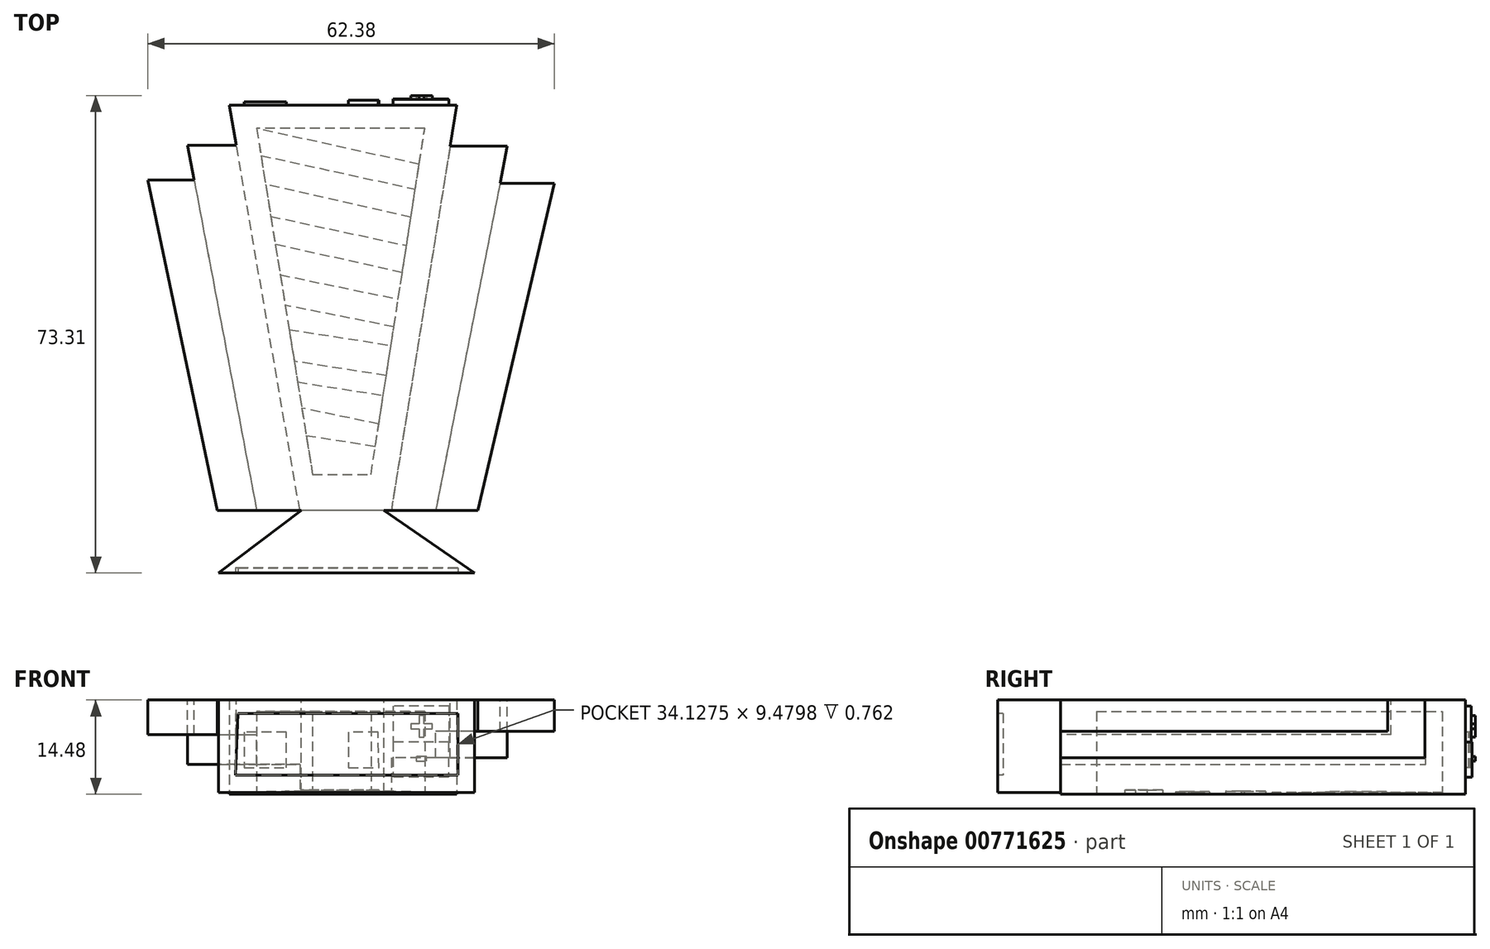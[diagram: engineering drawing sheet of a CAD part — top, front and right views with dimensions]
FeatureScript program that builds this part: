
annotation { "Feature Type Name" : "Feature", "Feature Type Description" : "" }
export const myFeature = defineFeature(function(context is Context, id is Id, definition is map)
    precondition{}
    {
        {
            var Q0;
            Q0=qCreatedBy(makeId("Top.planeOp"),FACE);
            var sketch = newSketch(context, id + "F0", { "sketchPlane" : qUnion([Q0])});
            skLineSegment(sketch, "E0", {"start": v(-16.97, 22.28) * mm, "end": v(17.92, 22.28) * mm});
            skLineSegment(sketch, "E1", {"start": v(17.92, 22.28) * mm, "end": v(7.87, -39.91) * mm});
            skLineSegment(sketch, "E2", {"start": v(7.87, -39.91) * mm, "end": v(-6.16, -39.91) * mm});
            skLineSegment(sketch, "E3", {"start": v(-6.16, -39.91) * mm, "end": v(-16.97, 22.28) * mm});
            skSolve(sketch);
        }
        {
            var Q0;
            Q0 = qSketchRegion(id + "F0", true);
            extrude(context, id + "F1", {"entities" : qUnion([Q0]), "depth" : 14.48 * mm, "offsetDistance" : 25.4 * mm});
        }
        {
            var Q0;
            Q0=makeQuery(id+"F1.opExtrude","CAP_FACE",FACE,{"disambiguationData":[OSD([sQuery(id+"F0.wireOp",EDGE,"E0"),sQuery(id+"F0.wireOp",EDGE,"E1"),sQuery(id+"F0.wireOp",EDGE,"E2"),sQuery(id+"F0.wireOp",EDGE,"E3")])],"isStart":false});
            var sketch = newSketch(context, id + "F2", { "sketchPlane" : qUnion([Q0])});
            skLineSegment(sketch, "E4", {"start": v(-15.9, 16.16) * mm, "end": v(-23.42, 16.16) * mm});
            skLineSegment(sketch, "E5", {"start": v(-23.42, 16.16) * mm, "end": v(-12.8, -39.91) * mm});
            skLineSegment(sketch, "E6", {"start": v(-12.8, -39.91) * mm, "end": v(-6.16, -39.91) * mm});
            skLineSegment(sketch, "E7", {"start": v(-6.16, -39.91) * mm, "end": v(-15.9, 16.16) * mm});
            skSolve(sketch);
        }
        {
            var Q0;
            Q0 = qSketchRegion(id + "F2", true);
            extrude(context, id + "F3", {"entities" : qUnion([Q0]), "operationType" : NewBodyOperationType.ADD, "oppositeDirection" : true, "depth" : 9.9 * mm, "offsetDistance" : 25.4 * mm});
        }
        {
            var Q0;
            Q0=makeQuery(id+"F3.boolean.opBoolean","MERGE",FACE,{"derivedFrom":[makeQuery(id+"F1.opExtrude","CAP_FACE",FACE,{"disambiguationData":[OSD([sQuery(id+"F0.wireOp",EDGE,"E0"),sQuery(id+"F0.wireOp",EDGE,"E1"),sQuery(id+"F0.wireOp",EDGE,"E2"),sQuery(id+"F0.wireOp",EDGE,"E3")])],"isStart":false}),makeQuery(id+"F3.opExtrude","CAP_FACE",FACE,{"disambiguationData":[OSD([sQuery(id+"F2.wireOp",EDGE,"E4"),sQuery(id+"F2.wireOp",EDGE,"E5"),sQuery(id+"F2.wireOp",EDGE,"E6"),sQuery(id+"F2.wireOp",EDGE,"E7")])],"isStart":true})]});
            var sketch = newSketch(context, id + "F4", { "sketchPlane" : qUnion([Q0])});
            skLineSegment(sketch, "E8", {"start": v(16.9, 16.03) * mm, "end": v(25.7, 16.03) * mm});
            skLineSegment(sketch, "E9", {"start": v(25.7, 16.03) * mm, "end": v(14.7, -39.91) * mm});
            skLineSegment(sketch, "E10", {"start": v(14.7, -39.91) * mm, "end": v(7.87, -39.91) * mm});
            skLineSegment(sketch, "E11", {"start": v(7.87, -39.91) * mm, "end": v(16.9, 16.03) * mm});
            skSolve(sketch);
        }
        {
            var Q0;
            Q0 = qSketchRegion(id + "F4", true);
            extrude(context, id + "F5", {"entities" : qUnion([Q0]), "operationType" : NewBodyOperationType.ADD, "oppositeDirection" : true, "depth" : 8.9 * mm, "offsetDistance" : 25.4 * mm});
        }
        {
            var Q0;
            Q0=makeQuery(id+"F5.boolean.opBoolean","MERGE",FACE,{"derivedFrom":[makeQuery(id+"F3.boolean.opBoolean","MERGE",FACE,{"derivedFrom":[makeQuery(id+"F1.opExtrude","CAP_FACE",FACE,{"disambiguationData":[OSD([sQuery(id+"F0.wireOp",EDGE,"E0"),sQuery(id+"F0.wireOp",EDGE,"E1"),sQuery(id+"F0.wireOp",EDGE,"E2"),sQuery(id+"F0.wireOp",EDGE,"E3")])],"isStart":false}),makeQuery(id+"F3.opExtrude","CAP_FACE",FACE,{"disambiguationData":[OSD([sQuery(id+"F2.wireOp",EDGE,"E4"),sQuery(id+"F2.wireOp",EDGE,"E5"),sQuery(id+"F2.wireOp",EDGE,"E6"),sQuery(id+"F2.wireOp",EDGE,"E7")])],"isStart":true})]}),makeQuery(id+"F5.opExtrude","CAP_FACE",FACE,{"disambiguationData":[OSD([sQuery(id+"F4.wireOp",EDGE,"E8"),sQuery(id+"F4.wireOp",EDGE,"E9"),sQuery(id+"F4.wireOp",EDGE,"E10"),sQuery(id+"F4.wireOp",EDGE,"E11")])],"isStart":true})]});
            var sketch = newSketch(context, id + "F6", { "sketchPlane" : qUnion([Q0])});
            skLineSegment(sketch, "E12", {"start": v(-22.4, 10.83) * mm, "end": v(-29.48, 10.83) * mm});
            skLineSegment(sketch, "E13", {"start": v(-29.48, 10.83) * mm, "end": v(-18.86, -39.91) * mm});
            skLineSegment(sketch, "E14", {"start": v(-18.86, -39.91) * mm, "end": v(-12.8, -39.91) * mm});
            skLineSegment(sketch, "E15", {"start": v(-12.8, -39.91) * mm, "end": v(-22.4, 10.83) * mm});
            skSolve(sketch);
        }
        {
            var Q0;
            Q0 = qSketchRegion(id + "F6", true);
            extrude(context, id + "F7", {"entities" : qUnion([Q0]), "operationType" : NewBodyOperationType.ADD, "oppositeDirection" : true, "depth" : 5.33 * mm, "offsetDistance" : 25.4 * mm});
        }
        {
            var Q0;
            Q0=makeQuery(id+"F7.boolean.opBoolean","MERGE",FACE,{"derivedFrom":[makeQuery(id+"F5.boolean.opBoolean","MERGE",FACE,{"derivedFrom":[makeQuery(id+"F3.boolean.opBoolean","MERGE",FACE,{"derivedFrom":[makeQuery(id+"F1.opExtrude","CAP_FACE",FACE,{"disambiguationData":[OSD([sQuery(id+"F0.wireOp",EDGE,"E0"),sQuery(id+"F0.wireOp",EDGE,"E1"),sQuery(id+"F0.wireOp",EDGE,"E2"),sQuery(id+"F0.wireOp",EDGE,"E3")])],"isStart":false}),makeQuery(id+"F3.opExtrude","CAP_FACE",FACE,{"disambiguationData":[OSD([sQuery(id+"F2.wireOp",EDGE,"E4"),sQuery(id+"F2.wireOp",EDGE,"E5"),sQuery(id+"F2.wireOp",EDGE,"E6"),sQuery(id+"F2.wireOp",EDGE,"E7")])],"isStart":true})]}),makeQuery(id+"F5.opExtrude","CAP_FACE",FACE,{"disambiguationData":[OSD([sQuery(id+"F4.wireOp",EDGE,"E8"),sQuery(id+"F4.wireOp",EDGE,"E9"),sQuery(id+"F4.wireOp",EDGE,"E10"),sQuery(id+"F4.wireOp",EDGE,"E11")])],"isStart":true})]}),makeQuery(id+"F7.opExtrude","CAP_FACE",FACE,{"disambiguationData":[OSD([sQuery(id+"F6.wireOp",EDGE,"E12"),sQuery(id+"F6.wireOp",EDGE,"E13"),sQuery(id+"F6.wireOp",EDGE,"E14"),sQuery(id+"F6.wireOp",EDGE,"E15")])],"isStart":true})]});
            var sketch = newSketch(context, id + "F8", { "sketchPlane" : qUnion([Q0])});
            skLineSegment(sketch, "E16", {"start": v(24.57, 10.33) * mm, "end": v(32.9, 10.33) * mm});
            skLineSegment(sketch, "E17", {"start": v(32.9, 10.33) * mm, "end": v(21.14, -39.91) * mm});
            skLineSegment(sketch, "E18", {"start": v(21.14, -39.91) * mm, "end": v(14.7, -39.91) * mm});
            skLineSegment(sketch, "E19", {"start": v(14.7, -39.91) * mm, "end": v(24.57, 10.33) * mm});
            skSolve(sketch);
        }
        {
            var Q0;
            Q0 = qSketchRegion(id + "F8", true);
            extrude(context, id + "F9", {"entities" : qUnion([Q0]), "operationType" : NewBodyOperationType.ADD, "oppositeDirection" : true, "depth" : 4.83 * mm, "offsetDistance" : 25.4 * mm});
        }
        {
            var Q0;
            Q0=makeQuery(id+"F1.opExtrude","CAP_FACE",FACE,{"disambiguationData":[OSD([sQuery(id+"F0.wireOp",EDGE,"E0"),sQuery(id+"F0.wireOp",EDGE,"E1"),sQuery(id+"F0.wireOp",EDGE,"E2"),sQuery(id+"F0.wireOp",EDGE,"E3")])],"isStart":true});
            var sketch = newSketch(context, id + "F10", { "sketchPlane" : qUnion([Q0])});
            skLineSegment(sketch, "E20", {"start": v(13.01, -18.72) * mm, "end": v(-12.8, -18.72) * mm});
            skLineSegment(sketch, "E21", {"start": v(-12.8, -18.72) * mm, "end": v(-4.21, 34.38) * mm});
            skLineSegment(sketch, "E22", {"start": v(-4.21, 34.38) * mm, "end": v(4.76, 34.38) * mm});
            skLineSegment(sketch, "E23", {"start": v(4.76, 34.38) * mm, "end": v(13.01, -18.72) * mm});
            skSolve(sketch);
        }
        {
            var Q0;
            Q0 = qSketchRegion(id + "F10", true);
            extrude(context, id + "F11", {"entities" : qUnion([Q0]), "operationType" : NewBodyOperationType.REMOVE, "oppositeDirection" : true, "depth" : 12.7 * mm, "offsetDistance" : 25.4 * mm});
        }
        {
            var Q0;
            Q0=makeQuery(id+"F1.opExtrude","CAP_FACE",FACE,{"disambiguationData":[OSD([sQuery(id+"F0.wireOp",EDGE,"E0"),sQuery(id+"F0.wireOp",EDGE,"E1"),sQuery(id+"F0.wireOp",EDGE,"E2"),sQuery(id+"F0.wireOp",EDGE,"E3")])],"isStart":true});
            var sketch = newSketch(context, id + "F12", { "sketchPlane" : qUnion([Q0])});
            skLineSegment(sketch, "E24", {"start": v(12.16, -13.22) * mm, "end": v(-12.8, -18.72) * mm});
            skLineSegment(sketch, "E25", {"start": v(-12.8, -18.72) * mm, "end": v(-12.14, -14.58) * mm});
            skLineSegment(sketch, "E26", {"start": v(-12.14, -14.58) * mm, "end": v(11.57, -9.4) * mm});
            skLineSegment(sketch, "E27", {"start": v(11.57, -9.4) * mm, "end": v(12.16, -13.22) * mm});
            skSolve(sketch);
        }
        {
            var Q0;
            Q0 = qSketchRegion(id + "F12", true);
            extrude(context, id + "F13", {"entities" : qUnion([Q0]), "operationType" : NewBodyOperationType.ADD, "oppositeDirection" : true, "depth" : 0.25 * mm, "offsetDistance" : 25.4 * mm});
        }
        {
            var Q0;
            Q0=makeQuery(id+"F13.boolean.opBoolean","MERGE",FACE,{"derivedFrom":[makeQuery(id+"F1.opExtrude","CAP_FACE",FACE,{"disambiguationData":[OSD([sQuery(id+"F0.wireOp",EDGE,"E0"),sQuery(id+"F0.wireOp",EDGE,"E1"),sQuery(id+"F0.wireOp",EDGE,"E2"),sQuery(id+"F0.wireOp",EDGE,"E3")])],"isStart":true}),makeQuery(id+"F13.opExtrude","CAP_FACE",FACE,{"disambiguationData":[OSD([sQuery(id+"F12.wireOp",EDGE,"E24"),sQuery(id+"F12.wireOp",EDGE,"E25"),sQuery(id+"F12.wireOp",EDGE,"E26"),sQuery(id+"F12.wireOp",EDGE,"E27")])],"isStart":true})]});
            var sketch = newSketch(context, id + "F14", { "sketchPlane" : qUnion([Q0])});
            skLineSegment(sketch, "E28", {"start": v(10.9, -5.07) * mm, "end": v(-11.42, -10.11) * mm});
            skLineSegment(sketch, "E29", {"start": v(-11.42, -10.11) * mm, "end": v(-10.63, -5.23) * mm});
            skLineSegment(sketch, "E30", {"start": v(-10.63, -5.23) * mm, "end": v(10.22, -0.75) * mm});
            skLineSegment(sketch, "E31", {"start": v(10.22, -0.75) * mm, "end": v(10.9, -5.07) * mm});
            skSolve(sketch);
        }
        {
            var Q0;
            Q0 = qSketchRegion(id + "F14", true);
            extrude(context, id + "F15", {"entities" : qUnion([Q0]), "operationType" : NewBodyOperationType.ADD, "oppositeDirection" : true, "depth" : 0.43 * mm, "offsetDistance" : 25.4 * mm});
        }
        {
            var Q0;
            Q0=makeQuery(id+"F15.boolean.opBoolean","MERGE",FACE,{"derivedFrom":[makeQuery(id+"F13.boolean.opBoolean","MERGE",FACE,{"derivedFrom":[makeQuery(id+"F1.opExtrude","CAP_FACE",FACE,{"disambiguationData":[OSD([sQuery(id+"F0.wireOp",EDGE,"E0"),sQuery(id+"F0.wireOp",EDGE,"E1"),sQuery(id+"F0.wireOp",EDGE,"E2"),sQuery(id+"F0.wireOp",EDGE,"E3")])],"isStart":true}),makeQuery(id+"F13.opExtrude","CAP_FACE",FACE,{"disambiguationData":[OSD([sQuery(id+"F12.wireOp",EDGE,"E24"),sQuery(id+"F12.wireOp",EDGE,"E25"),sQuery(id+"F12.wireOp",EDGE,"E26"),sQuery(id+"F12.wireOp",EDGE,"E27")])],"isStart":true})]}),makeQuery(id+"F15.opExtrude","CAP_FACE",FACE,{"disambiguationData":[OSD([sQuery(id+"F14.wireOp",EDGE,"E28"),sQuery(id+"F14.wireOp",EDGE,"E29"),sQuery(id+"F14.wireOp",EDGE,"E30"),sQuery(id+"F14.wireOp",EDGE,"E31")])],"isStart":true})]});
            var sketch = newSketch(context, id + "F16", { "sketchPlane" : qUnion([Q0])});
            skLineSegment(sketch, "E32", {"start": v(9.57, 3.4) * mm, "end": v(-9.93, -0.91) * mm});
            skLineSegment(sketch, "E33", {"start": v(-9.93, -0.91) * mm, "end": v(-9.17, 3.75) * mm});
            skLineSegment(sketch, "E34", {"start": v(-9.17, 3.75) * mm, "end": v(8.94, 7.49) * mm});
            skLineSegment(sketch, "E35", {"start": v(8.94, 7.49) * mm, "end": v(9.57, 3.4) * mm});
            skSolve(sketch);
        }
        {
            var Q0;
            Q0 = qSketchRegion(id + "F16", true);
            extrude(context, id + "F17", {"entities" : qUnion([Q0]), "operationType" : NewBodyOperationType.ADD, "oppositeDirection" : true, "depth" : 0.25 * mm, "offsetDistance" : 25.4 * mm});
        }
        {
            var Q0;
            Q0=makeQuery(id+"F17.boolean.opBoolean","MERGE",FACE,{"derivedFrom":[makeQuery(id+"F15.boolean.opBoolean","MERGE",FACE,{"derivedFrom":[makeQuery(id+"F13.boolean.opBoolean","MERGE",FACE,{"derivedFrom":[makeQuery(id+"F1.opExtrude","CAP_FACE",FACE,{"disambiguationData":[OSD([sQuery(id+"F0.wireOp",EDGE,"E0"),sQuery(id+"F0.wireOp",EDGE,"E1"),sQuery(id+"F0.wireOp",EDGE,"E2"),sQuery(id+"F0.wireOp",EDGE,"E3")])],"isStart":true}),makeQuery(id+"F13.opExtrude","CAP_FACE",FACE,{"disambiguationData":[OSD([sQuery(id+"F12.wireOp",EDGE,"E24"),sQuery(id+"F12.wireOp",EDGE,"E25"),sQuery(id+"F12.wireOp",EDGE,"E26"),sQuery(id+"F12.wireOp",EDGE,"E27")])],"isStart":true})]}),makeQuery(id+"F15.opExtrude","CAP_FACE",FACE,{"disambiguationData":[OSD([sQuery(id+"F14.wireOp",EDGE,"E28"),sQuery(id+"F14.wireOp",EDGE,"E29"),sQuery(id+"F14.wireOp",EDGE,"E30"),sQuery(id+"F14.wireOp",EDGE,"E31")])],"isStart":true})]}),makeQuery(id+"F17.opExtrude","CAP_FACE",FACE,{"disambiguationData":[OSD([sQuery(id+"F16.wireOp",EDGE,"E32"),sQuery(id+"F16.wireOp",EDGE,"E33"),sQuery(id+"F16.wireOp",EDGE,"E34"),sQuery(id+"F16.wireOp",EDGE,"E35")])],"isStart":true})]});
            var sketch = newSketch(context, id + "F18", { "sketchPlane" : qUnion([Q0])});
            skLineSegment(sketch, "E36", {"start": v(8.28, 11.74) * mm, "end": v(-8.41, 8.43) * mm});
            skLineSegment(sketch, "E37", {"start": v(-8.41, 8.43) * mm, "end": v(-7.81, 12.15) * mm});
            skLineSegment(sketch, "E38", {"start": v(-7.81, 12.15) * mm, "end": v(7.84, 14.58) * mm});
            skLineSegment(sketch, "E39", {"start": v(7.84, 14.58) * mm, "end": v(8.28, 11.74) * mm});
            skSolve(sketch);
        }
        {
            var Q0;
            Q0 = qSketchRegion(id + "F18", true);
            extrude(context, id + "F19", {"entities" : qUnion([Q0]), "operationType" : NewBodyOperationType.ADD, "oppositeDirection" : true, "depth" : 0.46 * mm, "offsetDistance" : 25.4 * mm});
        }
        {
            var Q0;
            Q0=makeQuery(id+"F19.boolean.opBoolean","MERGE",FACE,{"derivedFrom":[makeQuery(id+"F17.boolean.opBoolean","MERGE",FACE,{"derivedFrom":[makeQuery(id+"F15.boolean.opBoolean","MERGE",FACE,{"derivedFrom":[makeQuery(id+"F13.boolean.opBoolean","MERGE",FACE,{"derivedFrom":[makeQuery(id+"F1.opExtrude","CAP_FACE",FACE,{"disambiguationData":[OSD([sQuery(id+"F0.wireOp",EDGE,"E0"),sQuery(id+"F0.wireOp",EDGE,"E1"),sQuery(id+"F0.wireOp",EDGE,"E2"),sQuery(id+"F0.wireOp",EDGE,"E3")])],"isStart":true}),makeQuery(id+"F13.opExtrude","CAP_FACE",FACE,{"disambiguationData":[OSD([sQuery(id+"F12.wireOp",EDGE,"E24"),sQuery(id+"F12.wireOp",EDGE,"E25"),sQuery(id+"F12.wireOp",EDGE,"E26"),sQuery(id+"F12.wireOp",EDGE,"E27")])],"isStart":true})]}),makeQuery(id+"F15.opExtrude","CAP_FACE",FACE,{"disambiguationData":[OSD([sQuery(id+"F14.wireOp",EDGE,"E28"),sQuery(id+"F14.wireOp",EDGE,"E29"),sQuery(id+"F14.wireOp",EDGE,"E30"),sQuery(id+"F14.wireOp",EDGE,"E31")])],"isStart":true})]}),makeQuery(id+"F17.opExtrude","CAP_FACE",FACE,{"disambiguationData":[OSD([sQuery(id+"F16.wireOp",EDGE,"E32"),sQuery(id+"F16.wireOp",EDGE,"E33"),sQuery(id+"F16.wireOp",EDGE,"E34"),sQuery(id+"F16.wireOp",EDGE,"E35")])],"isStart":true})]}),makeQuery(id+"F19.opExtrude","CAP_FACE",FACE,{"disambiguationData":[OSD([sQuery(id+"F18.wireOp",EDGE,"E36"),sQuery(id+"F18.wireOp",EDGE,"E37"),sQuery(id+"F18.wireOp",EDGE,"E38"),sQuery(id+"F18.wireOp",EDGE,"E39")])],"isStart":true})]});
            var sketch = newSketch(context, id + "F20", { "sketchPlane" : qUnion([Q0])});
            skLineSegment(sketch, "E40", {"start": v(7.12, 19.22) * mm, "end": v(-7.02, 17.02) * mm});
            skLineSegment(sketch, "E41", {"start": v(-7.02, 17.02) * mm, "end": v(-6.5, 20.2) * mm});
            skLineSegment(sketch, "E42", {"start": v(-6.5, 20.2) * mm, "end": v(6.65, 22.25) * mm});
            skLineSegment(sketch, "E43", {"start": v(6.65, 22.25) * mm, "end": v(7.12, 19.22) * mm});
            skSolve(sketch);
        }
        {
            var Q0;
            Q0 = qSketchRegion(id + "F20", true);
            extrude(context, id + "F21", {"entities" : qUnion([Q0]), "operationType" : NewBodyOperationType.ADD, "oppositeDirection" : true, "depth" : 0.43 * mm, "offsetDistance" : 25.4 * mm});
        }
        {
            var Q0;
            Q0=makeQuery(id+"F21.boolean.opBoolean","MERGE",FACE,{"derivedFrom":[makeQuery(id+"F19.boolean.opBoolean","MERGE",FACE,{"derivedFrom":[makeQuery(id+"F17.boolean.opBoolean","MERGE",FACE,{"derivedFrom":[makeQuery(id+"F15.boolean.opBoolean","MERGE",FACE,{"derivedFrom":[makeQuery(id+"F13.boolean.opBoolean","MERGE",FACE,{"derivedFrom":[makeQuery(id+"F1.opExtrude","CAP_FACE",FACE,{"disambiguationData":[OSD([sQuery(id+"F0.wireOp",EDGE,"E0"),sQuery(id+"F0.wireOp",EDGE,"E1"),sQuery(id+"F0.wireOp",EDGE,"E2"),sQuery(id+"F0.wireOp",EDGE,"E3")])],"isStart":true}),makeQuery(id+"F13.opExtrude","CAP_FACE",FACE,{"disambiguationData":[OSD([sQuery(id+"F12.wireOp",EDGE,"E24"),sQuery(id+"F12.wireOp",EDGE,"E25"),sQuery(id+"F12.wireOp",EDGE,"E26"),sQuery(id+"F12.wireOp",EDGE,"E27")])],"isStart":true})]}),makeQuery(id+"F15.opExtrude","CAP_FACE",FACE,{"disambiguationData":[OSD([sQuery(id+"F14.wireOp",EDGE,"E28"),sQuery(id+"F14.wireOp",EDGE,"E29"),sQuery(id+"F14.wireOp",EDGE,"E30"),sQuery(id+"F14.wireOp",EDGE,"E31")])],"isStart":true})]}),makeQuery(id+"F17.opExtrude","CAP_FACE",FACE,{"disambiguationData":[OSD([sQuery(id+"F16.wireOp",EDGE,"E32"),sQuery(id+"F16.wireOp",EDGE,"E33"),sQuery(id+"F16.wireOp",EDGE,"E34"),sQuery(id+"F16.wireOp",EDGE,"E35")])],"isStart":true})]}),makeQuery(id+"F19.opExtrude","CAP_FACE",FACE,{"disambiguationData":[OSD([sQuery(id+"F18.wireOp",EDGE,"E36"),sQuery(id+"F18.wireOp",EDGE,"E37"),sQuery(id+"F18.wireOp",EDGE,"E38"),sQuery(id+"F18.wireOp",EDGE,"E39")])],"isStart":true})]}),makeQuery(id+"F21.opExtrude","CAP_FACE",FACE,{"disambiguationData":[OSD([sQuery(id+"F20.wireOp",EDGE,"E40"),sQuery(id+"F20.wireOp",EDGE,"E41"),sQuery(id+"F20.wireOp",EDGE,"E42"),sQuery(id+"F20.wireOp",EDGE,"E43")])],"isStart":true})]});
            var sketch = newSketch(context, id + "F22", { "sketchPlane" : qUnion([Q0])});
            skLineSegment(sketch, "E44", {"start": v(5.96, 26.65) * mm, "end": v(-5.86, 24.22) * mm});
            skLineSegment(sketch, "E45", {"start": v(-5.86, 24.22) * mm, "end": v(-5.18, 28.41) * mm});
            skLineSegment(sketch, "E46", {"start": v(-5.18, 28.41) * mm, "end": v(5.43, 30.06) * mm});
            skLineSegment(sketch, "E47", {"start": v(5.43, 30.06) * mm, "end": v(5.96, 26.65) * mm});
            skSolve(sketch);
        }
        {
            var Q0;
            Q0 = qSketchRegion(id + "F22", true);
            extrude(context, id + "F23", {"entities" : qUnion([Q0]), "operationType" : NewBodyOperationType.ADD, "oppositeDirection" : true, "depth" : 0.63 * mm, "offsetDistance" : 25.4 * mm});
        }
        {
            var Q0;
            Q0=makeQuery(id+"F9.boolean.opBoolean","MERGE",FACE,{"derivedFrom":[makeQuery(id+"F7.boolean.opBoolean","MERGE",FACE,{"derivedFrom":[makeQuery(id+"F5.boolean.opBoolean","MERGE",FACE,{"derivedFrom":[makeQuery(id+"F3.boolean.opBoolean","MERGE",FACE,{"derivedFrom":[makeQuery(id+"F1.opExtrude","CAP_FACE",FACE,{"disambiguationData":[OSD([sQuery(id+"F0.wireOp",EDGE,"E0"),sQuery(id+"F0.wireOp",EDGE,"E1"),sQuery(id+"F0.wireOp",EDGE,"E2"),sQuery(id+"F0.wireOp",EDGE,"E3")])],"isStart":false}),makeQuery(id+"F3.opExtrude","CAP_FACE",FACE,{"disambiguationData":[OSD([sQuery(id+"F2.wireOp",EDGE,"E4"),sQuery(id+"F2.wireOp",EDGE,"E5"),sQuery(id+"F2.wireOp",EDGE,"E6"),sQuery(id+"F2.wireOp",EDGE,"E7")])],"isStart":true})]}),makeQuery(id+"F5.opExtrude","CAP_FACE",FACE,{"disambiguationData":[OSD([sQuery(id+"F4.wireOp",EDGE,"E8"),sQuery(id+"F4.wireOp",EDGE,"E9"),sQuery(id+"F4.wireOp",EDGE,"E10"),sQuery(id+"F4.wireOp",EDGE,"E11")])],"isStart":true})]}),makeQuery(id+"F7.opExtrude","CAP_FACE",FACE,{"disambiguationData":[OSD([sQuery(id+"F6.wireOp",EDGE,"E12"),sQuery(id+"F6.wireOp",EDGE,"E13"),sQuery(id+"F6.wireOp",EDGE,"E14"),sQuery(id+"F6.wireOp",EDGE,"E15")])],"isStart":true})]}),makeQuery(id+"F9.opExtrude","CAP_FACE",FACE,{"disambiguationData":[OSD([sQuery(id+"F8.wireOp",EDGE,"E16"),sQuery(id+"F8.wireOp",EDGE,"E17"),sQuery(id+"F8.wireOp",EDGE,"E18"),sQuery(id+"F8.wireOp",EDGE,"E19")])],"isStart":true})]});
            var sketch = newSketch(context, id + "F24", { "sketchPlane" : qUnion([Q0])});
            skLineSegment(sketch, "E48", {"start": v(-5.97, -39.91) * mm, "end": v(-18.62, -49.53) * mm});
            skLineSegment(sketch, "E49", {"start": v(-18.62, -49.53) * mm, "end": v(20.68, -49.53) * mm});
            skLineSegment(sketch, "E50", {"start": v(20.68, -49.53) * mm, "end": v(6.73, -39.91) * mm});
            skLineSegment(sketch, "E51", {"start": v(6.73, -39.91) * mm, "end": v(-5.97, -39.91) * mm});
            skSolve(sketch);
        }
        {
            var Q0;
            Q0 = qSketchRegion(id + "F24", true);
            extrude(context, id + "F25", {"entities" : qUnion([Q0]), "operationType" : NewBodyOperationType.ADD, "oppositeDirection" : true, "depth" : 14.22 * mm, "offsetDistance" : 25.4 * mm});
        }
        {
            var Q0;
            Q0=makeQuery(id+"F25.opExtrude","SWEPT_FACE",FACE,{"disambiguationData":[OSD([sQuery(id+"F24.wireOp",EDGE,"E49")])]});
            var sketch = newSketch(context, id + "F26", { "sketchPlane" : qUnion([Q0])});
            skLineSegment(sketch, "E52", {"start": v(-15.64, 12.42) * mm, "end": v(18.1, 12.42) * mm});
            skLineSegment(sketch, "E53", {"start": v(18.1, 12.42) * mm, "end": v(18.1, 2.94) * mm});
            skLineSegment(sketch, "E54", {"start": v(18.1, 2.94) * mm, "end": v(-16.02, 2.94) * mm});
            skLineSegment(sketch, "E55", {"start": v(-15.64, 12.42) * mm, "end": v(-16.02, 2.94) * mm});
            skSolve(sketch);
        }
        {
            var Q0;
            Q0 = qSketchRegion(id + "F26", true);
            extrude(context, id + "F27", {"entities" : qUnion([Q0]), "operationType" : NewBodyOperationType.REMOVE, "oppositeDirection" : true, "depth" : 0.76 * mm, "offsetDistance" : 25.4 * mm});
        }
        {
            var Q0;
            Q0=makeQuery(id+"F1.opExtrude","SWEPT_FACE",FACE,{"disambiguationData":[OSD([sQuery(id+"F0.wireOp",EDGE,"E0")])]});
            var sketch = newSketch(context, id + "F28", { "sketchPlane" : qUnion([Q0])});
            skLineSegment(sketch, "E56", {"start": v(-5.84, 9.54) * mm, "end": v(-1.3, 9.54) * mm});
            skLineSegment(sketch, "E57", {"start": v(-1.3, 9.54) * mm, "end": v(-1.3, 4.08) * mm});
            skLineSegment(sketch, "E58", {"start": v(-1.3, 4.08) * mm, "end": v(-5.97, 4.08) * mm});
            skLineSegment(sketch, "E59", {"start": v(-5.97, 4.08) * mm, "end": v(-5.84, 9.54) * mm});
            skSolve(sketch);
        }
        {
            var Q0;
            Q0 = qSketchRegion(id + "F28", true);
            extrude(context, id + "F29", {"entities" : qUnion([Q0]), "operationType" : NewBodyOperationType.ADD, "depth" : 0.76 * mm, "offsetDistance" : 25.4 * mm});
        }
        {
            var Q0;
            Q0=makeQuery(id+"F1.opExtrude","SWEPT_FACE",FACE,{"disambiguationData":[OSD([sQuery(id+"F0.wireOp",EDGE,"E0")])]});
            var sketch = newSketch(context, id + "F30", { "sketchPlane" : qUnion([Q0])});
            skLineSegment(sketch, "E60", {"start": v(8.25, 9.57) * mm, "end": v(14.7, 9.57) * mm});
            skLineSegment(sketch, "E61", {"start": v(14.7, 9.57) * mm, "end": v(14.7, 4.08) * mm});
            skLineSegment(sketch, "E62", {"start": v(14.7, 4.08) * mm, "end": v(8.25, 4.08) * mm});
            skLineSegment(sketch, "E63", {"start": v(8.25, 4.08) * mm, "end": v(8.25, 9.57) * mm});
            skSolve(sketch);
        }
        {
            var Q0;
            Q0 = qSketchRegion(id + "F30", true);
            extrude(context, id + "F31", {"entities" : qUnion([Q0]), "operationType" : NewBodyOperationType.ADD, "depth" : 0.5 * mm, "offsetDistance" : 25.4 * mm});
        }
        {
            var Q0;
            Q0=makeQuery(id+"F1.opExtrude","SWEPT_FACE",FACE,{"disambiguationData":[OSD([sQuery(id+"F0.wireOp",EDGE,"E0")])]});
            var sketch = newSketch(context, id + "F32", { "sketchPlane" : qUnion([Q0])});
            skLineSegment(sketch, "E64.bottom", {"start": v(-16.7, 13.52) * mm, "end": v(-8.17, 13.52) * mm});
            skLineSegment(sketch, "E64.top", {"start": v(-16.7, 8) * mm, "end": v(-8.17, 8) * mm});
            skLineSegment(sketch, "E64.left", {"start": v(-16.7, 13.52) * mm, "end": v(-16.7, 8) * mm});
            skLineSegment(sketch, "E64.right", {"start": v(-8.17, 13.52) * mm, "end": v(-8.17, 8) * mm});
            skSolve(sketch);
        }
        {
            var Q0;
            Q0=makeQuery(id+"F32.imprint","IMPRINT",FACE,{"disambiguationData":[TD([[makeQuery(id+"F32.imprint","IMPRINT",EDGE,{"derivedFrom":sQuery(id+"F32.wireOp",EDGE,"E64.bottom")}),1.0]])]});
            var sketch = newSketch(context, id + "F33", { "sketchPlane" : qUnion([Q0])});
            skLineSegment(sketch, "E65.bottom", {"start": v(-16.67, 8.03) * mm, "end": v(-8.17, 8.03) * mm});
            skLineSegment(sketch, "E65.top", {"start": v(-16.67, 2.61) * mm, "end": v(-8.17, 2.61) * mm});
            skLineSegment(sketch, "E65.left", {"start": v(-16.67, 8.03) * mm, "end": v(-16.67, 2.61) * mm});
            skLineSegment(sketch, "E65.right", {"start": v(-8.17, 8.03) * mm, "end": v(-8.17, 2.61) * mm});
            skSolve(sketch);
        }
        {
            var Q0;
            Q0=makeQuery(id+"F32.imprint","IMPRINT",FACE,{"disambiguationData":[TD([[makeQuery(id+"F32.imprint","IMPRINT",EDGE,{"derivedFrom":sQuery(id+"F32.wireOp",EDGE,"E64.bottom")}),-1.0]])]});
            extrude(context, id + "F34", {"entities" : qUnion([Q0]), "operationType" : NewBodyOperationType.ADD, "depth" : 0.89 * mm, "offsetDistance" : 25.4 * mm});
        }
        {
            var Q0;
            {var subQ2=sQuery(id+"F33.wireOp",EDGE,"E65.top");Q0=makeQuery(id+"F33.imprint","IMPRINT",FACE,{"disambiguationData":[TD([[makeQuery(id+"F33.imprint","IMPRINT",EDGE,{"derivedFrom":subQ2}),1.0]])]});}
            extrude(context, id + "F35", {"entities" : qUnion([Q0]), "operationType" : NewBodyOperationType.ADD, "depth" : 0.97 * mm, "offsetDistance" : 25.4 * mm});
        }
        {
            var Q0;
            Q0=makeQuery(id+"F34.opExtrude","CAP_FACE",FACE,{"disambiguationData":[OSD([sQuery(id+"F32.wireOp",EDGE,"E64.bottom"),sQuery(id+"F32.wireOp",EDGE,"E64.top"),sQuery(id+"F32.wireOp",EDGE,"E64.left"),sQuery(id+"F32.wireOp",EDGE,"E64.right")])],"isStart":false});
            var sketch = newSketch(context, id + "F36", { "sketchPlane" : qUnion([Q0])});
            skText(sketch, "E66", { "text": "+", "fontName": "OpenSans-Bold.ttf"});
            const initialGuessF36  = {"E66": [-0.0145, 0.008, 1, 0, 0.00497]};
            skSetInitialGuess(sketch, initialGuessF36);
            skSolve(sketch);
        }
        {
            var Q0;
            Q0 = qSketchRegion(id + "F36", true);
            extrude(context, id + "F37", {"entities" : qUnion([Q0]), "operationType" : NewBodyOperationType.ADD, "depth" : 0.6 * mm, "offsetDistance" : 25.4 * mm});
        }
        {
            var Q0;
            Q0=makeQuery(id+"F35.opExtrude","CAP_FACE",FACE,{"disambiguationData":[OSD([sQuery(id+"F32.wireOp",EDGE,"E64.top"),sQuery(id+"F32.wireOp",EDGE,"E64.right"),sQuery(id+"F33.wireOp",EDGE,"E65.bottom"),sQuery(id+"F33.wireOp",EDGE,"E65.top"),sQuery(id+"F33.wireOp",EDGE,"E65.left"),sQuery(id+"F33.wireOp",EDGE,"E65.right")])],"isStart":false});
            var sketch = newSketch(context, id + "F38", { "sketchPlane" : qUnion([Q0])});
            skText(sketch, "E67", { "text": "-", "fontName": "OpenSans-Bold.ttf"});
            const initialGuessF38  = {"E67": [-0.01346, 0.00383, 1, 0, 0.00436]};
            skSetInitialGuess(sketch, initialGuessF38);
            skSolve(sketch);
        }
        {
            var Q0;
            Q0 = qSketchRegion(id + "F38", true);
            extrude(context, id + "F39", {"entities" : qUnion([Q0]), "operationType" : NewBodyOperationType.ADD, "depth" : 0.5 * mm, "offsetDistance" : 25.4 * mm});
        }
    });
